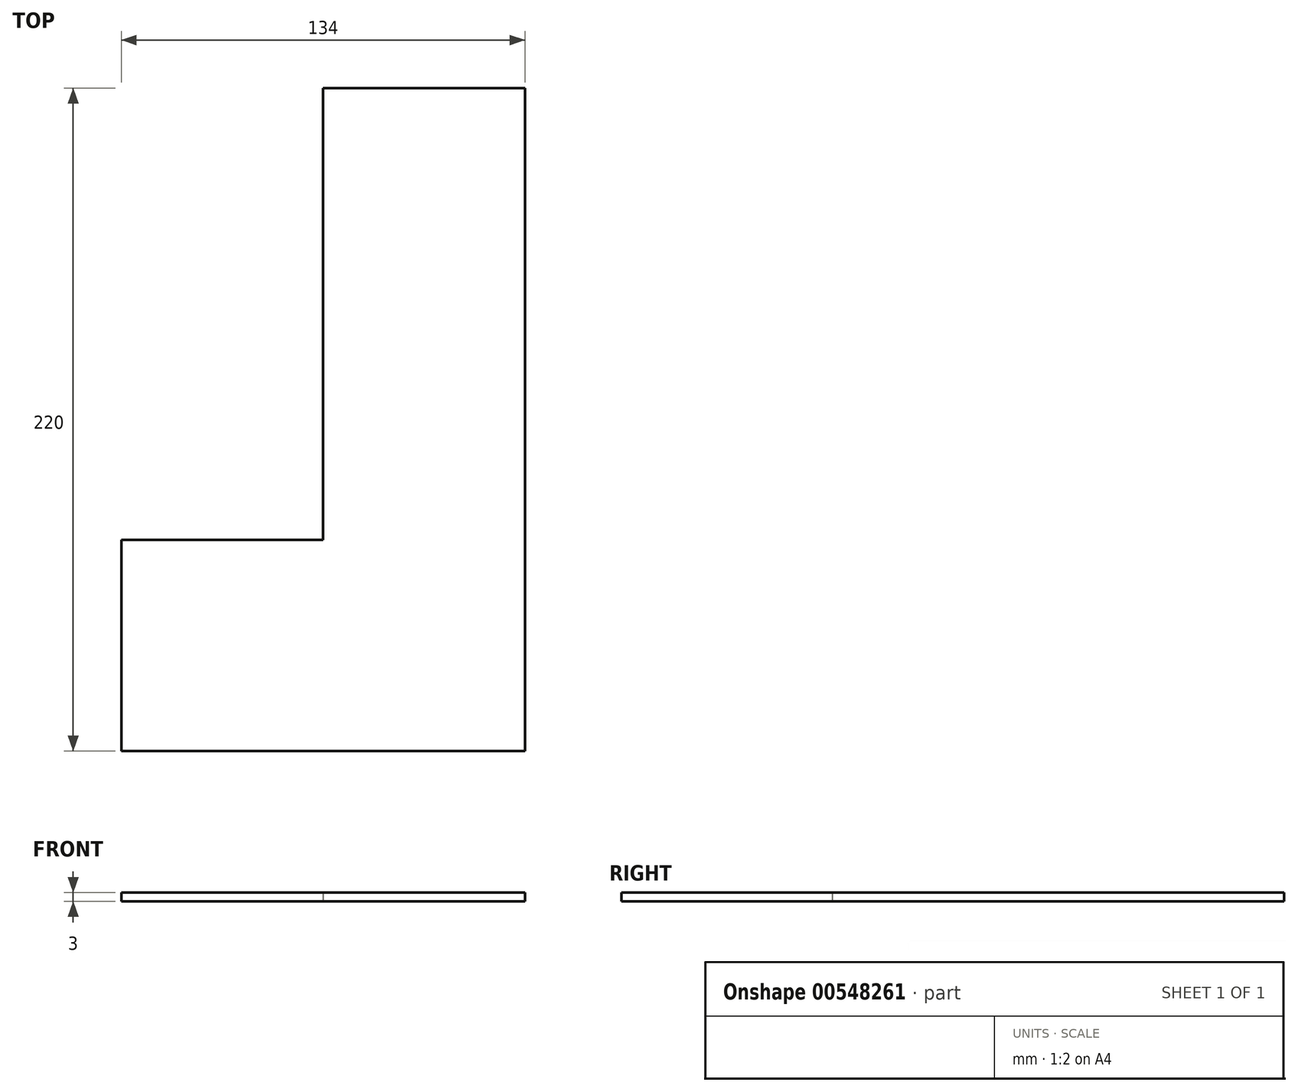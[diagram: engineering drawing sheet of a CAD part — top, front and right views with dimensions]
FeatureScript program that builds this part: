
annotation { "Feature Type Name" : "Feature", "Feature Type Description" : "" }
export const myFeature = defineFeature(function(context is Context, id is Id, definition is map)
    precondition{}
    {
        {
            var Q0;
            Q0=qCreatedBy(makeId("Top.planeOp"),FACE);
            var sketch = newSketch(context, id + "F0", { "sketchPlane" : qUnion([Q0])});
            skLineSegment(sketch, "E0.bottom", {"start": v(24.38, 122.44) * mm, "end": v(-42.62, 122.44) * mm});
            skLineSegment(sketch, "E0.top", {"start": v(24.38, -97.56) * mm, "end": v(-42.62, -97.56) * mm});
            skLineSegment(sketch, "E0.right", {"start": v(-42.62, 122.44) * mm, "end": v(-42.62, -27.56) * mm});
            skLineSegment(sketch, "E1.bottom", {"start": v(-42.62, -27.56) * mm, "end": v(-109.62, -27.56) * mm});
            skLineSegment(sketch, "E1.right", {"start": v(-109.62, -27.56) * mm, "end": v(-109.62, -97.56) * mm});
            skLineSegment(sketch, "E2", {"start": v(24.38, -97.56) * mm, "end": v(24.38, 122.44) * mm});
            skLineSegment(sketch, "E3", {"start": v(-42.62, -97.56) * mm, "end": v(-109.62, -97.56) * mm});
            skSolve(sketch);
        }
        {
            var Q0;
            Q0=makeQuery(id+"F0.imprint","IMPRINT",FACE,{"disambiguationData":[TD([[makeQuery(id+"F0.imprint","IMPRINT",EDGE,{"derivedFrom":sQuery(id+"F0.wireOp",EDGE,"E0.bottom")}),1.0]])]});
            extrude(context, id + "F1", {"entities" : qUnion([Q0]), "depth" : 3 * mm, "offsetDistance" : 25 * mm});
        }
    });
